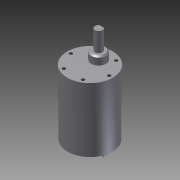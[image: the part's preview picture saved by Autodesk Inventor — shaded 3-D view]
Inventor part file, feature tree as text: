
AUTODESK INVENTOR PART (.ipt)
format: ipt  version: 2011 SP2 (Build 150309200, 309)  size: 163,328 bytes
history: native  units: mm
features: extrude x8, sketch x6, hole x1, pattern_circular x1, chamfer x1
ambient origin geometry x8: Origin, YZ Plane, XZ Plane, XY Plane, X Axis, Y Axis, Z Axis, Center Point
bodies: Solid1 (feature_tree)
feature tree (17):
  extrude  "Extrusion1"  Depth=22.0mm TaperAngle=0.0deg
  extrude  "Extrusion2"  Depth=30.0mm TaperAngle=0.0deg
  sketch  "Sketch3"  dims[d6=35.5mm d7=10.0mm]
  extrude  "Extrusion3"  Depth=10.0mm
  extrude  "Extrusion4"  Depth=4.0mm
  extrude  "Extrusion5"  Depth=1.0mm
  sketch  "Sketch4"  dims[d8=4.0mm d9=4.0mm]
  extrude  "Extrusion6"  Depth=2.0mm
  hole  "Hole1"  [1 undecoded]
  pattern_circular  "Circular Pattern1"  [2 undecoded]
  chamfer  "Chamfer1"  Distance=5.6mm
  extrude  "Extrusion7"  Depth=2.0mm TaperAngle=0.0deg
  extrude  "Extrusion8"  Depth=1.0mm TaperAngle=0.0deg
  sketch  "Sketch1"  dims[d0=36.8mm d1=22.0mm d2=0.0mm]
  sketch  "Sketch2"  dims[d3=36.0mm d4=30.0mm d5=0.0mm]
  sketch  "Sketch5"  dims[d10=1.0mm d11=1.0mm]
  sketch  "Sketch6"  dims[d12=2.0mm d13=2.0mm d14=12.0mm d15=12.0mm d16=5.6mm d17=0.0mm d18=2.0mm d19=0.0mm d20=1.0mm d21=0.0mm d22=7.0mm d23=12.0mm d24=6.5mm d25=0.0mm d28=15.5mm d29=2.621mm d30=7.0mm d31=4.0mm d32=2.0mm d33=90.0deg d34=8.0mm d35=20.594885mm d36=60.0mm d37=360.0deg d39=1.0mm d40=2.0mm d41=45.0deg d42=6.0mm d43=15.5mm d44=0.0mm d45=5.4mm d46=12.0mm d47=0.0mm]
note: 3 required parameter values undecoded (feature->parameter linkage not recoverable at this tier; creation-order binding heuristic only, values carry confidence <= 0.55)
